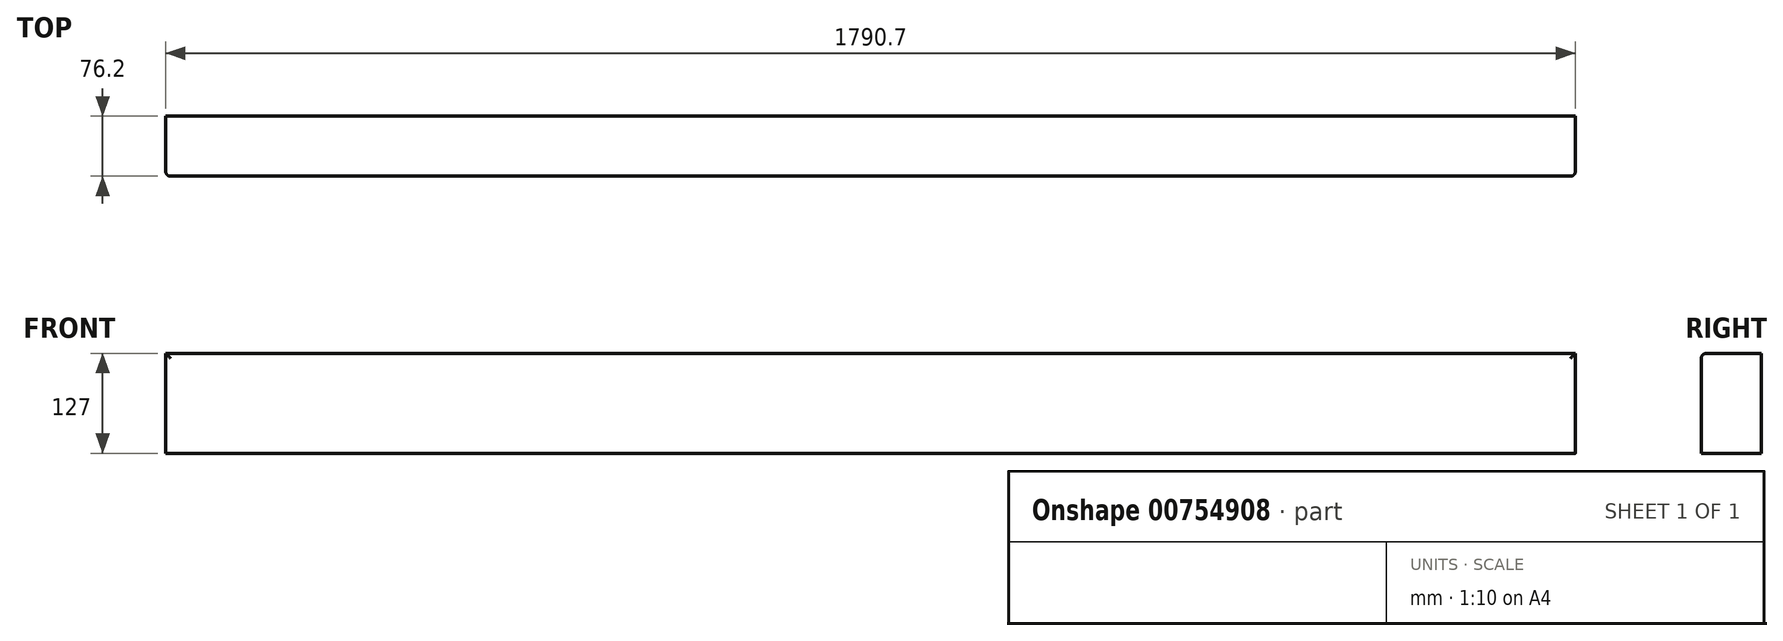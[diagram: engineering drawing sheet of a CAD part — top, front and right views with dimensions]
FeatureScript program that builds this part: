
annotation { "Feature Type Name" : "Feature", "Feature Type Description" : "" }
export const myFeature = defineFeature(function(context is Context, id is Id, definition is map)
    precondition{}
    {
        {
            var Q0;
            Q0=qCreatedBy(makeId("Front.planeOp"),FACE);
            var sketch = newSketch(context, id + "F0", { "sketchPlane" : qUnion([Q0])});
            skLineSegment(sketch, "E0.bottom", {"start": v(-895.35, 63.5) * mm, "end": v(895.35, 63.5) * mm});
            skLineSegment(sketch, "E0.top", {"start": v(-895.35, -63.5) * mm, "end": v(895.35, -63.5) * mm});
            skLineSegment(sketch, "E0.left", {"start": v(-895.35, 63.5) * mm, "end": v(-895.35, -63.5) * mm});
            skLineSegment(sketch, "E0.right", {"start": v(895.35, 63.5) * mm, "end": v(895.35, -63.5) * mm});
            skPoint(sketch, "E0.middle", {"position": v(0, 0) * mm});
            skSolve(sketch);
        }
        {
            var Q0;
            Q0=makeQuery(id+"F0.imprint","IMPRINT",FACE,{"disambiguationData":[TD([[makeQuery(id+"F0.imprint","IMPRINT",EDGE,{"derivedFrom":sQuery(id+"F0.wireOp",EDGE,"E0.bottom")}),-1.0]])]});
            extrude(context, id + "F1", {"entities" : qUnion([Q0]), "endBound" : BoundingType.SYMMETRIC, "depth" : 76.2 * mm});
        }
        {
            var Q0;
            Q0=makeQuery(id+"F1.opExtrude","CAP_EDGE",EDGE,{"disambiguationData":[OSD([sQuery(id+"F0.wireOp",EDGE,"E0.bottom")])],"isStart":false});
            var Q1;
            Q1=makeQuery(id+"F1.opExtrude","CAP_EDGE",EDGE,{"disambiguationData":[OSD([sQuery(id+"F0.wireOp",EDGE,"E0.right")])],"isStart":false});
            var Q2;
            Q2=makeQuery(id+"F1.opExtrude","CAP_EDGE",EDGE,{"disambiguationData":[OSD([sQuery(id+"F0.wireOp",EDGE,"E0.left")])],"isStart":false});
            fillet(context, id + "F2", {"entities" : qUnion([Q0, Q1, Q2]), "radius" : 6.35 * mm, "tangentPropagation" : true, "allowEdgeOverflow" : false});
        }
    });
